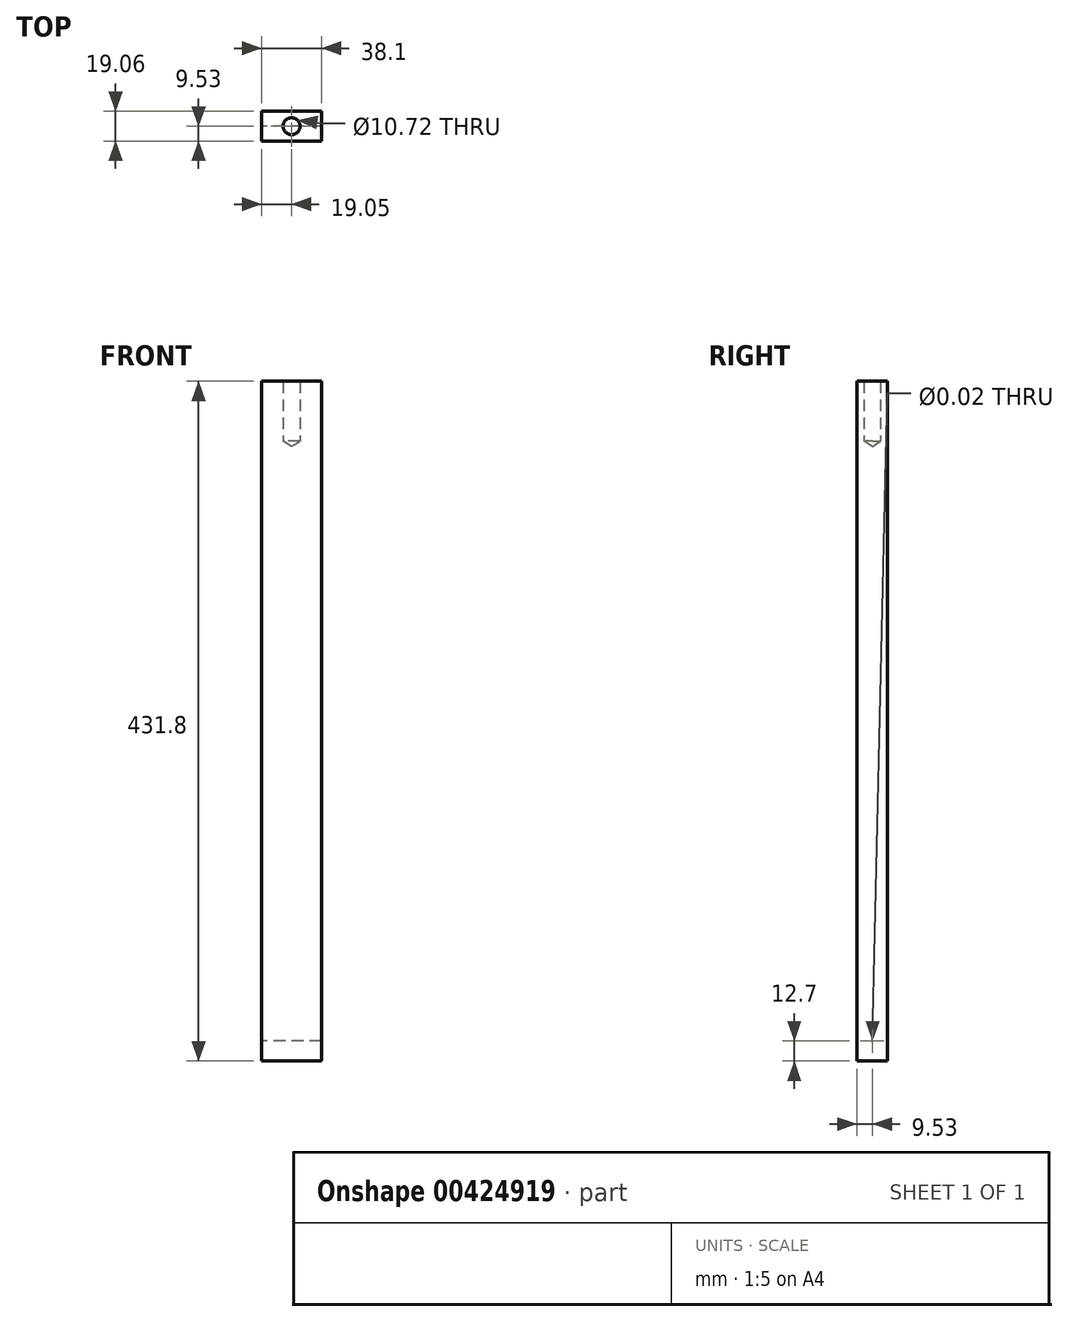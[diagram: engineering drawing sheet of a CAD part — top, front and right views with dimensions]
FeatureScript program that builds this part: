
annotation { "Feature Type Name" : "Feature", "Feature Type Description" : "" }
export const myFeature = defineFeature(function(context is Context, id is Id, definition is map)
    precondition{}
    {
        {
            var Q0;
            Q0=qCreatedBy(makeId("Front.planeOp"),FACE);
            var sketch = newSketch(context, id + "F0", { "sketchPlane" : qUnion([Q0])});
            skLineSegment(sketch, "E0.bottom", {"start": v(19.05, -215.9) * mm, "end": v(-19.05, -215.9) * mm});
            skLineSegment(sketch, "E0.top", {"start": v(19.05, 215.9) * mm, "end": v(-19.05, 215.9) * mm});
            skLineSegment(sketch, "E0.left", {"start": v(19.05, -215.9) * mm, "end": v(19.05, 215.9) * mm});
            skLineSegment(sketch, "E0.right", {"start": v(-19.05, -215.9) * mm, "end": v(-19.05, 215.9) * mm});
            skPoint(sketch, "E0.middle", {"position": v(0, 0) * mm});
            skSolve(sketch);
        }
        {
            var Q0;
            Q0 = qSketchRegion(id + "F0", true);
            extrude(context, id + "F1", {"entities" : qUnion([Q0]), "depth" : 19.05 * mm, "symmetric" : true});
        }
        {
            var Q0;
            Q0=makeQuery(id+"F1.opExtrude","SWEPT_FACE",FACE,{"disambiguationData":[OSD([sQuery(id+"F0.wireOp",EDGE,"E0.left")])]});
            var sketch = newSketch(context, id + "F2", { "sketchPlane" : qUnion([Q0])});
            skPoint(sketch, "E1", {"position": v(0, -203.2) * mm});
            skPoint(sketch, "E1.positionSnap0", {"position": v(0, -215.9) * mm});
            skSolve(sketch);
        }
        {
            var Q0;
            Q0=sQuery(id+"F2.wireOp",VERTEX,"E1");
            var Q1;
            Q1=makeQuery(id+"F1.opExtrude","SWEPT_BODY",BODY,{"disambiguationData":[OSD([sQuery(id+"F0.wireOp",EDGE,"E0.bottom"),sQuery(id+"F0.wireOp",EDGE,"E0.top"),sQuery(id+"F0.wireOp",EDGE,"E0.left"),sQuery(id+"F0.wireOp",EDGE,"E0.right")])]});
            hole(context, id + "F3", {"style" : HoleStyle.SIMPLE, "endStyle" : HoleEndStyle.THROUGH, "standardTappedOrClearance" : lookupTablePath({ "standard" : "ANSI", "size" : "1/2 (0.5)", "type" : "Drilled" }), "standardBlindInLast" : lookupTablePath({ "standard" : "ANSI", "size" : "1/2", "type" : "Drilled" }), "holeDiameter" : 1 / 50.8 * mm, "isTappedThrough" : true, "tappedDepth" : 32.23 * mm, "tapClearance" : 3, "locations" : qUnion([Q0]), "scope" : qUnion([Q1]), "startStyle" : HoleStartStyle.SKETCH});
        }
        {
            var Q0;
            Q0=makeQuery(id+"F1.opExtrude","SWEPT_FACE",FACE,{"disambiguationData":[OSD([sQuery(id+"F0.wireOp",EDGE,"E0.top")])]});
            var sketch = newSketch(context, id + "F4", { "sketchPlane" : qUnion([Q0])});
            skPoint(sketch, "E2", {"position": v(0, 0) * mm});
            skSolve(sketch);
        }
        {
            var Q0;
            Q0=sQuery(id+"F4.wireOp",VERTEX,"E2");
            var Q1;
            Q1=makeQuery(id+"F1.opExtrude","SWEPT_BODY",BODY,{"disambiguationData":[OSD([sQuery(id+"F0.wireOp",EDGE,"E0.bottom"),sQuery(id+"F0.wireOp",EDGE,"E0.top"),sQuery(id+"F0.wireOp",EDGE,"E0.left"),sQuery(id+"F0.wireOp",EDGE,"E0.right")])]});
            hole(context, id + "F5", {"style" : HoleStyle.SIMPLE, "endStyle" : HoleEndStyle.BLIND, "standardTappedOrClearance" : lookupTablePath({ "standard" : "ANSI", "engagement" : "75%", "pitch" : "13 tpi", "size" : "1/2", "type" : "Tapped" }), "standardBlindInLast" : lookupTablePath({ "standard" : "ANSI", "engagement" : "75%", "pitch" : "13 tpi", "size" : "1/2", "type" : "Tapped" }), "holeDiameter" : 10.72 * mm, "showTappedDepth" : true, "holeDepth" : 38.1 * mm, "isTappedThrough" : true, "tappedDepth" : 32.23 * mm, "tapClearance" : 3, "locations" : qUnion([Q0]), "scope" : qUnion([Q1]), "majorDiameter" : 12.7 * mm, "startStyle" : HoleStartStyle.SKETCH});
        }
    });
